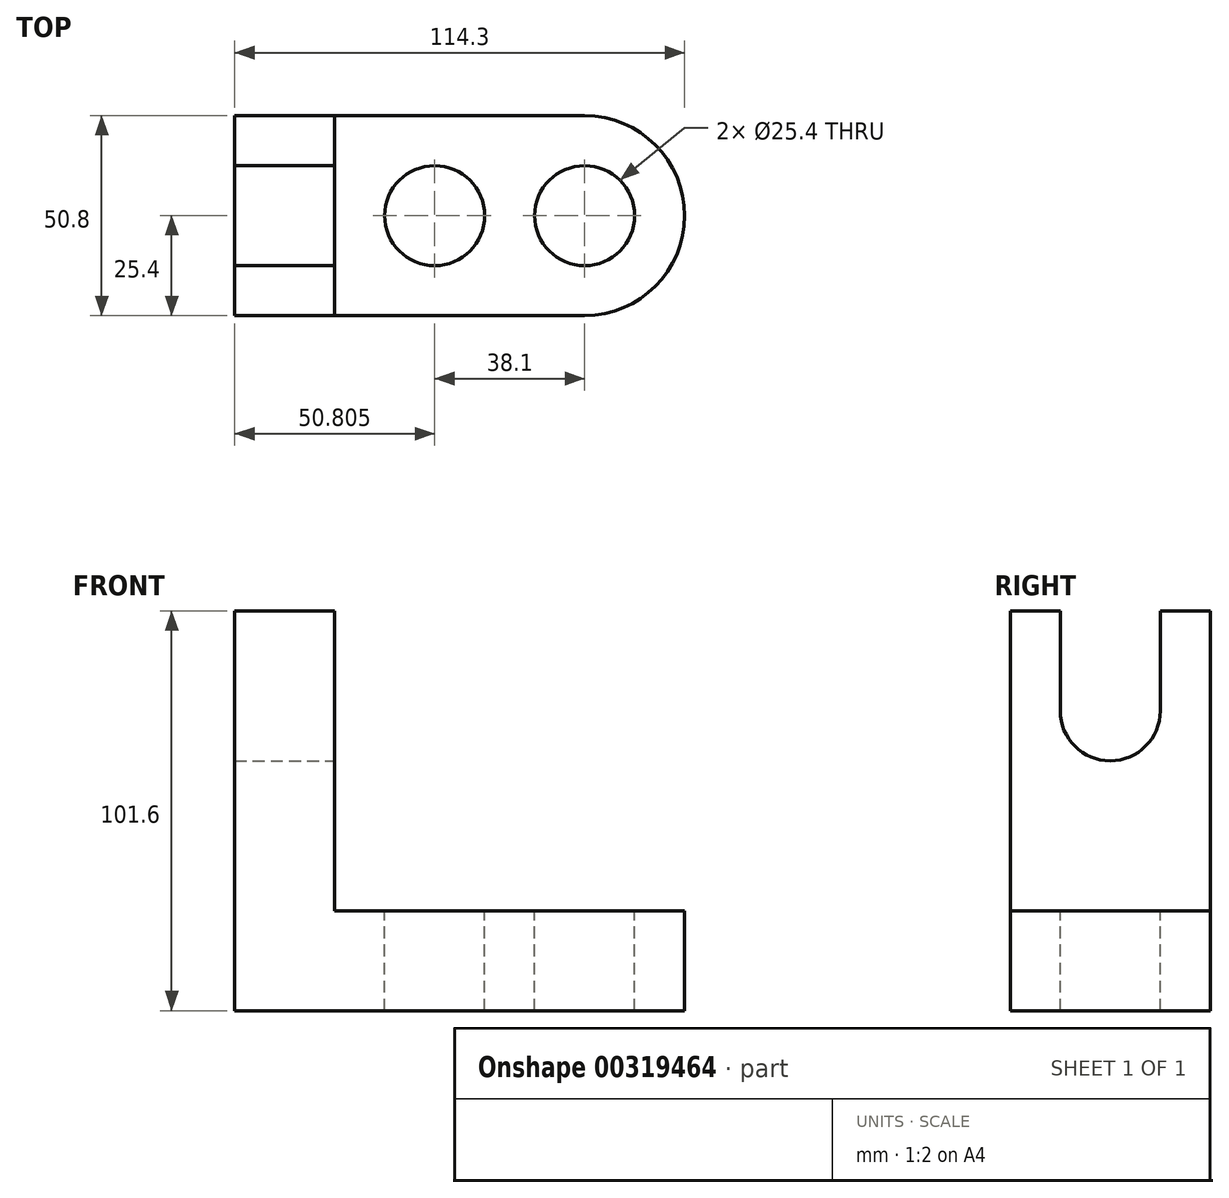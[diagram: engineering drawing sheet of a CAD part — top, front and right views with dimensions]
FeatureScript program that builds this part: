
annotation { "Feature Type Name" : "Feature", "Feature Type Description" : "" }
export const myFeature = defineFeature(function(context is Context, id is Id, definition is map)
    precondition{}
    {
        {
            var Q0;
            Q0=qCreatedBy(makeId("Front.planeOp"),FACE);
            var sketch = newSketch(context, id + "F0", { "sketchPlane" : qUnion([Q0])});
            skLineSegment(sketch, "E0", {"start": v(-62.39, 36.89) * mm, "end": v(-62.39, -64.71) * mm});
            skLineSegment(sketch, "E1", {"start": v(-62.39, -64.71) * mm, "end": v(64.61, -64.71) * mm});
            skLineSegment(sketch, "E2", {"start": v(64.61, -64.71) * mm, "end": v(64.61, -39.31) * mm});
            skLineSegment(sketch, "E3", {"start": v(64.61, -39.31) * mm, "end": v(-36.99, -39.31) * mm});
            skLineSegment(sketch, "E4", {"start": v(-36.99, -39.31) * mm, "end": v(-36.99, 36.89) * mm});
            skLineSegment(sketch, "E5", {"start": v(-36.99, 36.89) * mm, "end": v(-62.39, 36.89) * mm});
            skSolve(sketch);
        }
        {
            var Q0;
            Q0=makeQuery(id+"F0.imprint","IMPRINT",FACE,{"disambiguationData":[TD([[makeQuery(id+"F0.imprint","IMPRINT",EDGE,{"derivedFrom":sQuery(id+"F0.wireOp",EDGE,"E0")}),1.0]])]});
            extrude(context, id + "F1", {"entities" : qUnion([Q0]), "depth" : 50.8 * mm});
        }
        {
            var Q0;
            Q0=makeQuery(id+"F1.opExtrude","SWEPT_FACE",FACE,{"disambiguationData":[OSD([sQuery(id+"F0.wireOp",EDGE,"E3")])]});
            var sketch = newSketch(context, id + "F2", { "sketchPlane" : qUnion([Q0])});
            skArc(sketch, "E6", {"start": v(39.21, -50.8) * mm, "mid": v(64.61, -25.4) * mm, "end": v(39.21, 0) * mm});
            skPoint(sketch, "E6.centerSnap0", {"position": v(64.61, -25.4) * mm});
            skSolve(sketch);
        }
        {
            var Q0;
            {var subQ0=sQuery(id+"F2.wireOp",EDGE,"E6");var subQ1=sQuery(id+"F0.wireOp",EDGE,"E3");var subQ2=makeQuery(id+"F1.opExtrude","CAP_EDGE",EDGE,{"disambiguationData":[OSD([subQ1])],"isStart":false});var subQ3=makeQuery(id+"F2.imprint","INTERSECT",VERTEX,{"derivedFrom":[subQ2,subQ0]});Q0=makeQuery(id+"F2.imprint","IMPRINT",FACE,{"disambiguationData":[TD([[makeQuery(id+"F2.imprint","IMPRINT",EDGE,{"disambiguationData":[TD([[subQ3,-1.0]])],"derivedFrom":subQ0}),-1.0]])]});}
            var Q1;
            {var subQ0=sQuery(id+"F2.wireOp",EDGE,"E6");var subQ1=sQuery(id+"F0.wireOp",EDGE,"E3");var subQ2=makeQuery(id+"F1.opExtrude","CAP_EDGE",EDGE,{"disambiguationData":[OSD([subQ1])],"isStart":true});var subQ3=makeQuery(id+"F2.imprint","INTERSECT",VERTEX,{"derivedFrom":[subQ2,subQ0]});Q1=makeQuery(id+"F2.imprint","IMPRINT",FACE,{"disambiguationData":[TD([[makeQuery(id+"F2.imprint","IMPRINT",EDGE,{"disambiguationData":[TD([[subQ3,1.0]])],"derivedFrom":subQ0}),-1.0]])]});}
            extrude(context, id + "F3", {"entities" : qUnion([Q0, Q1]), "operationType" : NewBodyOperationType.REMOVE, "oppositeDirection" : true, "depth" : 25.4 * mm});
        }
        {
            var Q0;
            Q0=makeQuery(id+"F1.opExtrude","SWEPT_FACE",FACE,{"disambiguationData":[OSD([sQuery(id+"F0.wireOp",EDGE,"E3")])]});
            var sketch = newSketch(context, id + "F4", { "sketchPlane" : qUnion([Q0])});
            skCircle(sketch, "E7", {"center": v(39.21, -25.4) * mm, "radius": 12.7 * mm});
            skCircle(sketch, "E8", {"center": v(1.11, -25.4) * mm, "radius": 12.7 * mm});
            skSolve(sketch);
        }
        {
            var Q0;
            Q0=makeQuery(id+"F1.opExtrude","SWEPT_FACE",FACE,{"disambiguationData":[OSD([sQuery(id+"F0.wireOp",EDGE,"E4")])]});
            extrude(context, id + "F5", {"entities" : qUnion([Q0]), "operationType" : NewBodyOperationType.ADD, "depth" : 12.7 * mm});
        }
        {
            var Q0;
            Q0=makeQuery(id+"F1.opExtrude","SWEPT_FACE",FACE,{"disambiguationData":[OSD([sQuery(id+"F0.wireOp",EDGE,"E0")])]});
            extrude(context, id + "F6", {"entities" : qUnion([Q0]), "operationType" : NewBodyOperationType.REMOVE, "oppositeDirection" : true, "depth" : 12.7 * mm});
        }
        {
            var Q0;
            Q0=makeQuery(id+"F5.opExtrude","CAP_FACE",FACE,{"disambiguationData":[OSD([sQuery(id+"F0.wireOp",EDGE,"E4")])],"isStart":false});
            var sketch = newSketch(context, id + "F7", { "sketchPlane" : qUnion([Q0])});
            skArc(sketch, "E9", {"start": v(-38.1, 11.49) * mm, "mid": v(-25.4, -1.21) * mm, "end": v(-12.7, 11.49) * mm});
            skPoint(sketch, "E9.centerSnap0", {"position": v(-25.4, 36.89) * mm});
            skLineSegment(sketch, "E10", {"start": v(-38.1, 11.49) * mm, "end": v(-38.1, 36.89) * mm});
            skLineSegment(sketch, "E11", {"start": v(-12.7, 11.49) * mm, "end": v(-12.7, 36.89) * mm});
            skSolve(sketch);
        }
        {
            var Q0;
            Q0=makeQuery(id+"F7.imprint","IMPRINT",FACE,{"disambiguationData":[TD([[makeQuery(id+"F7.imprint","IMPRINT",EDGE,{"derivedFrom":sQuery(id+"F7.wireOp",EDGE,"E9")}),1.0]])]});
            extrude(context, id + "F8", {"entities" : qUnion([Q0]), "operationType" : NewBodyOperationType.REMOVE, "endBound" : BoundingType.THROUGH_ALL, "oppositeDirection" : true, "depth" : 25.4 * mm});
        }
        {
            var Q0;
            Q0=makeQuery(id+"F4.imprint","IMPRINT",FACE,{"disambiguationData":[TD([[makeQuery(id+"F4.imprint","IMPRINT",EDGE,{"derivedFrom":sQuery(id+"F4.wireOp",EDGE,"E8")}),1.0]])]});
            var Q1;
            Q1=makeQuery(id+"F4.imprint","IMPRINT",FACE,{"disambiguationData":[TD([[makeQuery(id+"F4.imprint","IMPRINT",EDGE,{"derivedFrom":sQuery(id+"F4.wireOp",EDGE,"E7")}),1.0]])]});
            extrude(context, id + "F9", {"entities" : qUnion([Q0, Q1]), "operationType" : NewBodyOperationType.REMOVE, "endBound" : BoundingType.THROUGH_ALL, "oppositeDirection" : true, "depth" : 25.4 * mm});
        }
    });
